# Revit family: Furniture_Table_STIKS-8.1
name_source: partatom
category: Furniture
units: mm (PartAtom-declared; Revit-internal decimal feet)

## family parameters
Always vertical = No
Cut with Voids When Loaded = No
OmniClass Number = 23.21.23.15.17
Render Appearance Source = Family Geometry
Room Calculation Point = No
Shared = No
Work Plane-Based = Yes

## types (6) — shared parameters
BIMobject category = Table
BIMobject category code = furniture-table
BIMobject main category = Furniture
BIMobject main category code = furniture
Brand url = https://www.sandlerseating.com
Description = Low table base 38cm / 15" on 4 solid oak legs. Available in oak or lacquered finishes.
Edition number = 1
Height = 380 mm
IFC Classification = Furnishing Element
Manufacturer = Sandler
Manufacturer country = USA
Manufacturer name = Sandler
Masterformat 2014 Code = 12 48 43.13
Masterformat 2014 Description = Table Mats
Model = STICKS 38
OmniClass Code = 23-21 23 15 17
Product Guid = ??
Product SKU = ??
Product data url = https://www.sandlerseating.com
Product family = Furniture
Product group = Table
Product name = STICKS 38
Product url = https://www.sandlerseating.com
QR code = https://www.sandlerseating.com
URL = https://www.sandlerseating.com
Uniformat II Description = Movable Furnishings
zero-valued in all types: Default Elevation

## per-type parameters (varying)
| type | Frame Material | Top Material | Top Type |
| STICKS 38 - TOP 24" Wood | Wood - Oak - Natural - V | Wood - Oak - Natural - V | IC_TT_Rnd_Wood : Wood Rnd Top 60 |
| STICKS 38 - TOP 28" Wood | Wood - Oak - Walnut | Wood - Black Walnut | IC_TT_Rnd_Wood : Wood Rnd Top 70 |
| STICKS 38 - TOP 32" Wood | Wood - Oak - Black - V | Wood - Oak - Wenge | IC_TT_Rnd_Wood : Wood Rnd Top 80 |
| STICKS 38 - TOP 24" Laminate | Wood - Oak - Natural - V | HPL - Black | IC_TT_Rnd_LAM : LAM Rnd Top 60 |
| STICKS 38 - TOP 28" Laminate | Wood - Oak - Wenge | HPL - Black | IC_TT_Rnd_LAM : LAM Rnd Top 70 |
| STICKS 38 - TOP 32" Laminate | Lacquer - W1 - B00 Black | HPL - White | IC_TT_Rnd_LAM : LAM Rnd Top 80 |

## geometry (parser evidence)
native form markers: Sweep x7
no freeform markers — native parametric forms only
